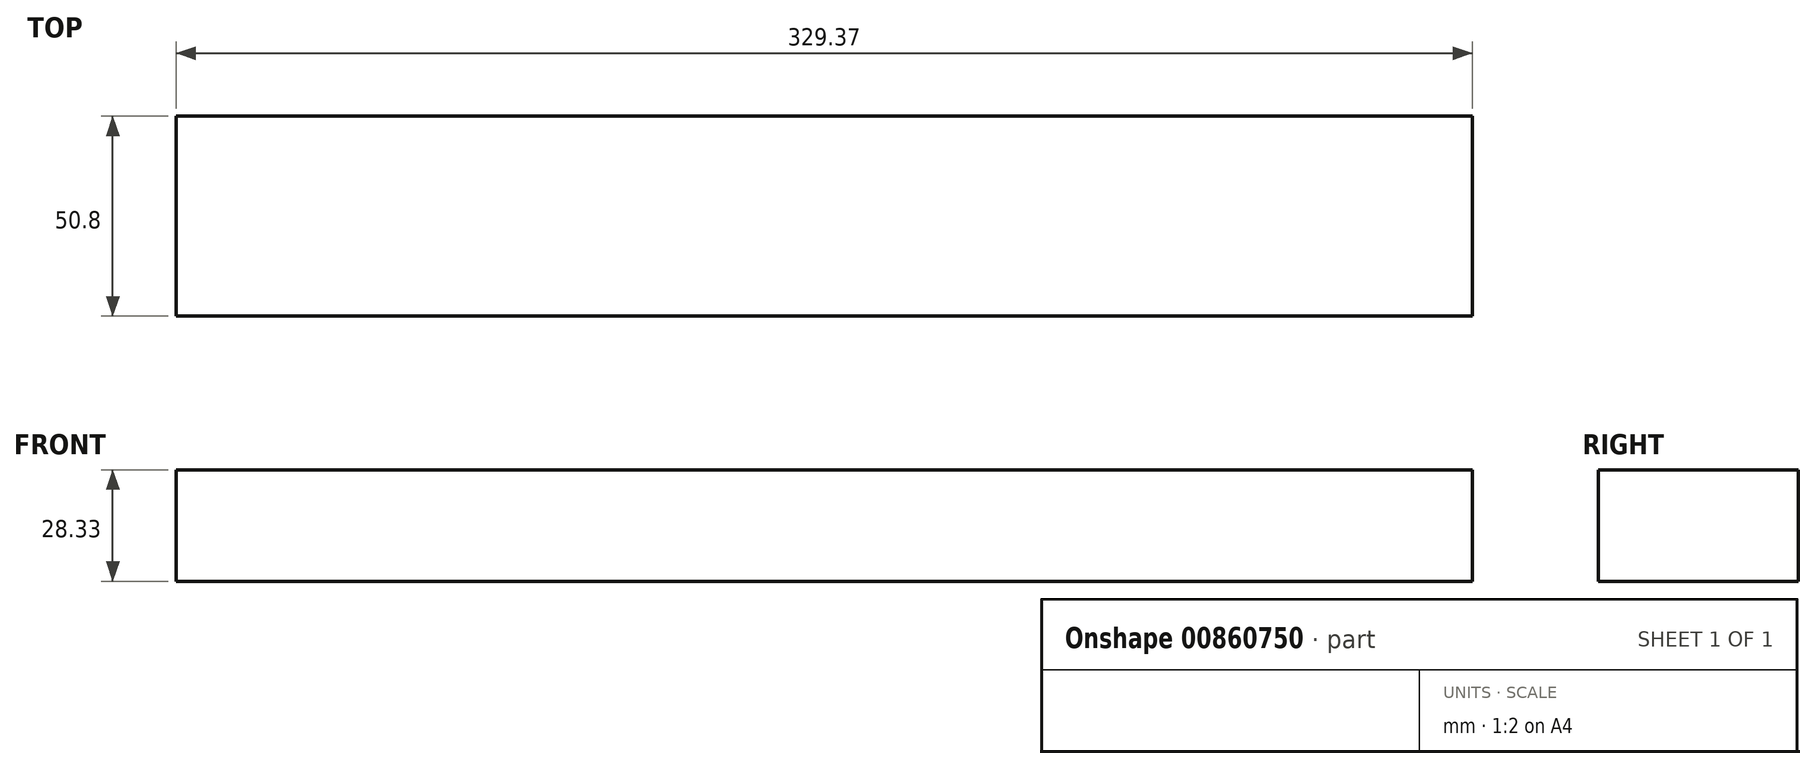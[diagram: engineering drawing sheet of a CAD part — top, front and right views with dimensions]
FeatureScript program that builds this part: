
annotation { "Feature Type Name" : "Feature", "Feature Type Description" : "" }
export const myFeature = defineFeature(function(context is Context, id is Id, definition is map)
    precondition{}
    {
        {
            var Q0;
            Q0=qCreatedBy(makeId("Front.planeOp"),FACE);
            var sketch = newSketch(context, id + "F0", { "sketchPlane" : qUnion([Q0])});
            skLineSegment(sketch, "E0", {"start": v(0, 0) * mm, "end": v(329.37, 0) * mm});
            skLineSegment(sketch, "E1", {"start": v(329.37, 0) * mm, "end": v(329.37, 28.33) * mm});
            skLineSegment(sketch, "E2", {"start": v(329.37, 28.33) * mm, "end": v(0, 28.33) * mm});
            skLineSegment(sketch, "E3", {"start": v(0, 28.33) * mm, "end": v(0, 0) * mm});
            skSolve(sketch);
        }
        {
            var Q0;
            Q0 = qSketchRegion(id + "F0", true);
            extrude(context, id + "F1", {"entities" : qUnion([Q0]), "depth" : 50.8 * mm, "offsetDistance" : 25.4 * mm});
        }
    });
